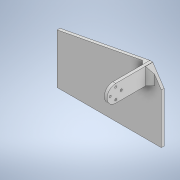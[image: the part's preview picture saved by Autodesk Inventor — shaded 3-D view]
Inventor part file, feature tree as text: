
AUTODESK INVENTOR PART (.ipt)
format: ipt  version: 2020 (Build 240168000, 168)  size: 206,848 bytes
history: native  units: in
note: dims shown in document units (in); Inventor stores cm internally (conversion verified against a paired STEP export)
features: extrude x5, sketch x5, chamfer x2
ambient origin geometry x8: Origin, YZ Plane, XZ Plane, XY Plane, X Axis, Y Axis, Z Axis, Center Point
bodies: Solid1 (feature_tree)
feature tree (12):
  extrude  "Extrusion1"  Depth=1.2in
  extrude  "Extrusion2"  Depth=0.1406in
  extrude  "Extrusion3"  Depth=0.1406in
  extrude  "Extrusion4"  Depth=0.2in
  chamfer  "Chamfer1"  Distance=0.2in
  chamfer  "Chamfer2"  Distance=0.2in
  extrude  "Extrusion5"  Depth=6.5in
  sketch  "Sketch1"  dims[d0=1.2in d1=0.77in]
  sketch  "Sketch2"  dims[d3=0.1406in d4=0.1406in]
  sketch  "Sketch3"  dims[d5=0.1406in d6=0.1406in]
  sketch  "Sketch4"  dims[d7=0.2in d8=0.0in d9=2.4in]
  sketch  "Sketch5"  dims[d10=1.2in d11=0.2in d12=0.2in d13=0.0in d14=6.5in d15=0.2in d16=1.0in d17=3.5in d18=0.0in d19=0.2in d20=0.2in d21=0.0in d22=0.3125in d23=0.125in d24=45.0deg d25=0.3125in d26=0.125in d27=45.0deg d28=0.5in d29=6.7in d30=0.5in d31=0.5in d32=0.5in d33=3.5in d34=0.5in d35=4.0in d36=0.1in d37=0.0in]
